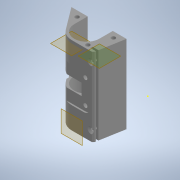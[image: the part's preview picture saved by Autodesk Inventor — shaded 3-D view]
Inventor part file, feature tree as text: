
AUTODESK INVENTOR PART (.ipt)
format: ipt  version: 2022 (Build 260153000, 153)  size: 512,512 bytes
history: native  units: mm
features: sketch x17, extrude x16, reference x16, projected_geometry x13, other x11, fillet x5, chamfer x2, mirror x2
ambient origin geometry x8: Origin, YZ Plane, XZ Plane, XY Plane, X Axis, Y Axis, Z Axis, Center Point
bodies: Body1 (feature_tree)
feature tree (82):
  other  "Твердое тело1"
  extrude  "Выдавливание1"  Depth=3.0mm
  extrude  "Выдавливание3"  Depth=3.0mm
  other  "РабПлоскость3"
  extrude  "Выдавливание4"  Depth=0.5mm
  other  "РабПлоскость6"
  extrude  "Выдавливание5"  Depth=0.5mm
  other  "РабПлоскость2"
  extrude  "Выдавливание6"  Depth=150.0mm
  fillet  "Сопряжение1"  Radius=81.0mm
  extrude  "Выдавливание7"  Depth=14.0mm TaperAngle=0.0deg
  chamfer  "Фаска1"  Distance=14.0mm
  chamfer  "Фаска2"  Distance=2.0mm
  extrude  "Выдавливание8"  Depth=2.0mm
  mirror  "Зеркальное отражение2"
  sketch  "Эскиз11"
  extrude  "Выдавливание10"  TaperAngle=0.0deg  [1 undecoded]
  extrude  "Выдавливание11"  Depth=2.0mm
  extrude  "Выдавливание12"  Depth=65.0mm
  extrude  "Выдавливание13"  Depth=2.2mm
  extrude  "Выдавливание14"  Depth=10.0mm TaperAngle=0.0deg
  extrude  "Выдавливание15"  Depth=300.0mm TaperAngle=0.0deg
  extrude  "Выдавливание16"  Depth=41.0mm
  extrude  "Выдавливание17"  Depth=81.0mm
  fillet  "Сопряжение2"  Radius=30.0mm
  fillet  "Сопряжение3"  Radius=30.0mm
  fillet  "Сопряжение4"  Radius=2.0mm
  mirror  "Зеркальное отражение3"
  fillet  "Сопряжение5"  Radius=3.0mm
  extrude  "Выдавливание18"  Depth=10.0mm
  sketch  "Эскиз1"
  reference  "Ссылка1"
  reference  "Ссылка2"
  reference  "Ссылка3"
  reference  "Ссылка4"
  reference  "Ссылка5"
  reference  "Ссылка6"
  reference  "Ссылка7"
  reference  "Ссылка8"
  reference  "Ссылка9"
  sketch  "Эскиз4"
  sketch  "Эскиз5"
  sketch  "Эскиз6"
  sketch  "Эскиз7"
  projected_geometry  "Спроецированная петля5"
  projected_geometry  "Спроецированная петля6"
  sketch  "Эскиз8"
  reference  "Ссылка17"
  projected_geometry  "Спроецированная петля7"
  sketch  "Эскиз9"
  reference  "Ссылка18"
  reference  "Ссылка19"
  reference  "Ссылка20"
  sketch  "Эскиз12"
  reference  "Ссылка23"
  sketch  "Эскиз13"
  sketch  "Эскиз15"
  projected_geometry  "Спроецированная петля13"
  sketch  "Эскиз16"
  projected_geometry  "Спроецированная петля14"
  projected_geometry  "Спроецированная петля15"
  projected_geometry  "Спроецированная петля16"
  sketch  "Эскиз17"
  reference  "Ссылка24"
  reference  "Ссылка25"
  sketch  "Эскиз18"
  projected_geometry  "Спроецированная петля19"
  sketch  "Эскиз19"
  projected_geometry  "Спроецированная петля20"
  sketch  "Эскиз20"
  projected_geometry  "Спроецированная петля21"
  projected_geometry  "Спроецированная петля22"
  projected_geometry  "Спроецированная петля23"
  projected_geometry  "Спроецированная петля24"
  sketch  "Эскиз21"
  other  "<userpath>\Documents\Git\MZCAT_2024\MZCAT.iam"
  other  "MZCAT.iam"
  other  "plan:1"
  other  "akkum_plate:1"
  other  "main_wheel_fixator:1"
  other  "CAT_protector:1"
  other  "base plate:2"
note: 1 required parameter value undecoded (feature->parameter linkage not recoverable at this tier; creation-order binding heuristic only, values carry confidence <= 0.55)
